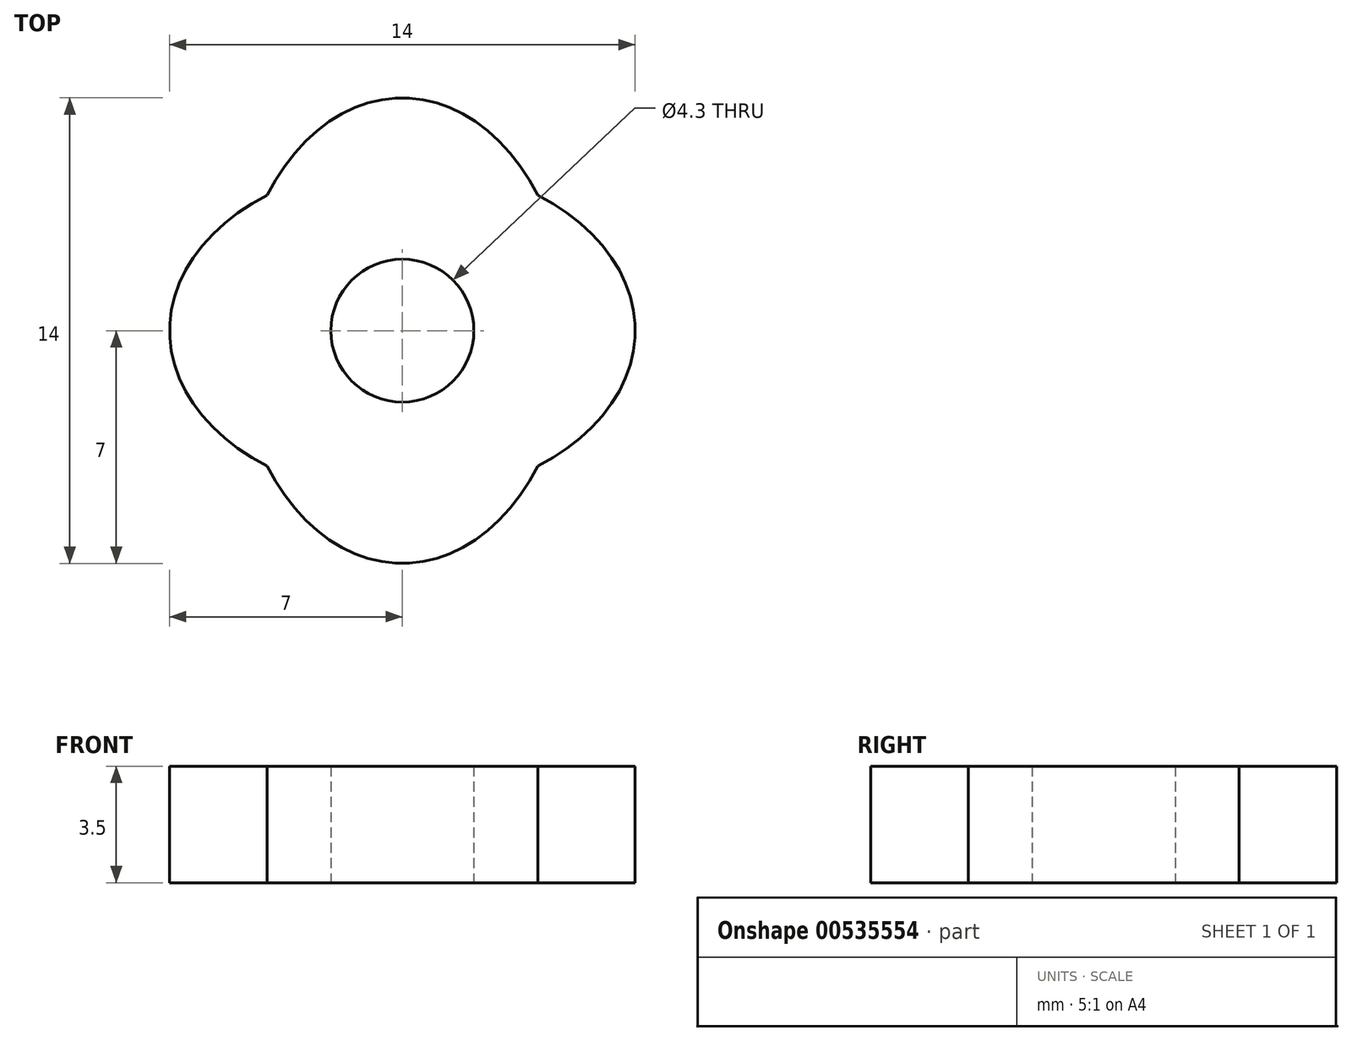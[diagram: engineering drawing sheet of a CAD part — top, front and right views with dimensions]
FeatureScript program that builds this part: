
annotation { "Feature Type Name" : "Feature", "Feature Type Description" : "" }
export const myFeature = defineFeature(function(context is Context, id is Id, definition is map)
    precondition{}
    {
        {
            var Q0;
            Q0=qCreatedBy(makeId("Top.planeOp"),FACE);
            var sketch = newSketch(context, id + "F0", { "sketchPlane" : qUnion([Q0])});
            skEllipse(sketch, "E0", {"center": v(0, 0) * mm, "majorRadius": 5 * mm, "minorRadius": 7 * mm, "majorAxis": v(-1, 0)});
            skCircle(sketch, "E1", {"center": v(0, 0) * mm, "radius": 2.15 * mm});
            skEllipse(sketch, "E2", {"center": v(0, 0) * mm, "majorRadius": 5 * mm, "minorRadius": 7 * mm, "majorAxis": v(0, 1)});
            skCircle(sketch, "E3", {"center": v(0, 0) * mm, "radius": 3.5 * mm});
            skSolve(sketch);
        }
        {
            var Q0;
            Q0 = qSketchRegion(id + "F0", true);
            var Q1;
            Q1=makeQuery(id+"F0.imprint","IMPRINT",FACE,{"disambiguationData":[TD([[makeQuery(id+"F0.imprint","IMPRINT",EDGE,{"derivedFrom":sQuery(id+"F0.wireOp",EDGE,"E1")}),-1.0]])]});
            extrude(context, id + "F1", {"entities" : qUnion([Q0, Q1]), "depth" : 3.5 * mm, "offsetDistance" : 25 * mm});
        }
    });
